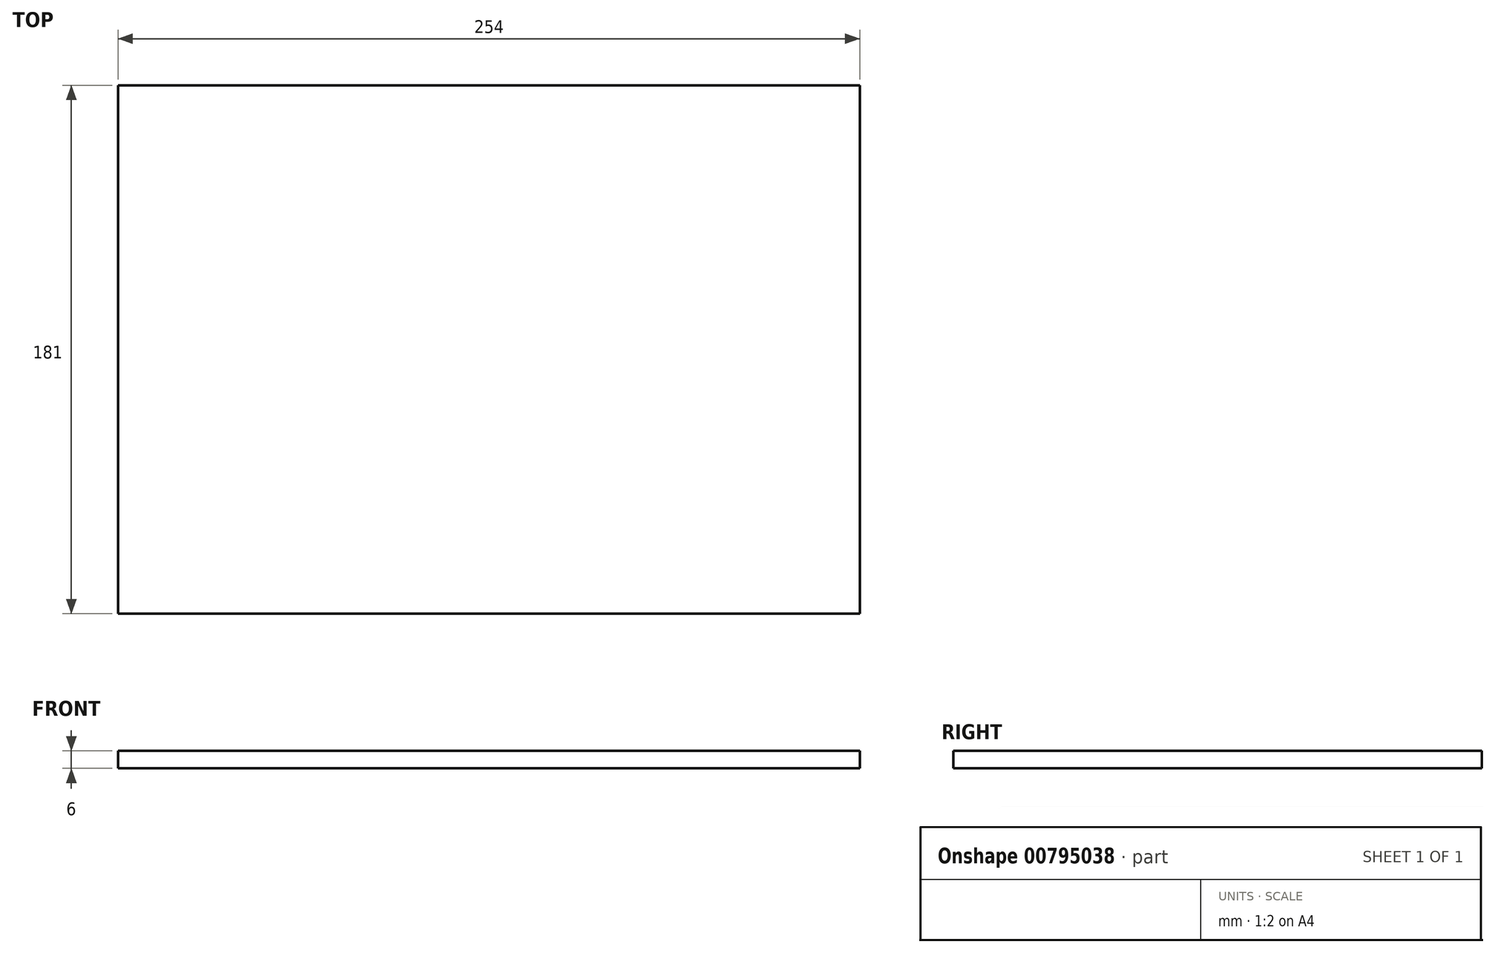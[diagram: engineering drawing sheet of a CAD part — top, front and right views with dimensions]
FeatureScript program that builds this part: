
annotation { "Feature Type Name" : "Feature", "Feature Type Description" : "" }
export const myFeature = defineFeature(function(context is Context, id is Id, definition is map)
    precondition{}
    {
        {
            var Q0;
            Q0=qCreatedBy(makeId("Top.planeOp"),FACE);
            var sketch = newSketch(context, id + "F0", { "sketchPlane" : qUnion([Q0])});
            skLineSegment(sketch, "E0.bottom", {"start": v(127, 90.5) * mm, "end": v(-127, 90.5) * mm});
            skLineSegment(sketch, "E0.top", {"start": v(127, -90.5) * mm, "end": v(-127, -90.5) * mm});
            skLineSegment(sketch, "E0.left", {"start": v(127, 90.5) * mm, "end": v(127, -90.5) * mm});
            skLineSegment(sketch, "E0.right", {"start": v(-127, 90.5) * mm, "end": v(-127, -90.5) * mm});
            skPoint(sketch, "E0.middle", {"position": v(0, 0) * mm});
            skSolve(sketch);
        }
        {
            var Q0;
            Q0=makeQuery(id+"F0.imprint","IMPRINT",FACE,{"disambiguationData":[TD([[makeQuery(id+"F0.imprint","IMPRINT",EDGE,{"derivedFrom":sQuery(id+"F0.wireOp",EDGE,"E0.bottom")}),1.0]])]});
            extrude(context, id + "F1", {"entities" : qUnion([Q0]), "depth" : 6 * mm, "offsetDistance" : 25 * mm});
        }
    });
